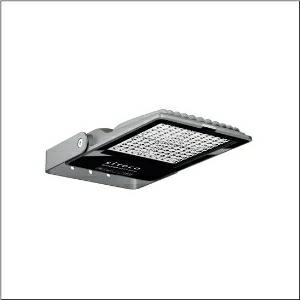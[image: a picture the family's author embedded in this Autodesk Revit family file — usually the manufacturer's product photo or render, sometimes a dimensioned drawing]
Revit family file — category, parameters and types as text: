
# Revit family: sicompact_r__31_mini___pl32_5xa7571b1k23_124a
name_source: partatom
category: Lighting Fixtures
units: mm (PartAtom-declared; Revit-internal decimal feet)

## family parameters
Cut with Voids When Loaded = No
Host = Face
Light Source = No
Part Type = Normal
Room Calculation Point = No
Round Connector Dimension = Use Diameter
Shared = No

## types (1)
- SiCompact® 31 mini  PL32 (1 x LED, 8000 lm, 48 W, 3000K)
    Apparent Load = 48 VA
    CIE Flux Codes = 32 69 98 100 100
    Color Rendering = 70
    Color Temperature = 3000K
    Default Elevation = 1800 mm
    Description = SiCompact® 31 mini, floodlight, primary light control with lens, of plastic, of toughened safety glass, transparent, light distribution: PL32, light emission: direct distribution, primary light characteristic: asymmetric, installation type: surface-mounted, LED, High Power LED, rated luminous flux: 8.000lm, luminous efficacy: 167lm/W, light colour: 730, colour temperature: 3000K, control gear: ON/OFF, with cable, 3x 1.5mm², mains connection: 220..240V, AC, 50/60Hz, connection cable pre-assembled, cable length: 2m, rated input power: 48W, of diecast aluminium, specular, metallic grey (RAL 9006), length: 461mm, width: 261mm, height: 62mm, bracket, of sheet steel, coated, metallic grey (RAL 9006), ON/OFF, protection rating (complete): IP66, insulation class (complete): insulation class I (protective earthing), certification: CE, ENEC, impact resistance: IK08, permissible operating ambient temperature: -40..+45°C, packaging unit: 1 piece

Light Distribution: PL32
    Height = 62 mm
    Lamp = 1 x LED
    Lamp Light Flux = 8000 lm
    Lamp Power = 48 W
    Lamp count = 1
    Length = 460 mm
    Luminous efficacy = 167 lm/W
    Manufacturer = Siteco
    ModVariant = No
    Model = 5XA7571B1K23
    Mounting Place = Wall
    Mounting Type = Surface mounted
    Number of Poles = 1
    OnlyDefault = Yes
    Power Factor = 1
    Product Name = SiCompact® 31 mini | PL32
    Product group = floodlight | wall mounted
    ProductGroupID = 2001
    Protection Class = Protection class I
    Protection Degree = IP 66
    RLX_Detail_Level = 1
    RLX_Emergency_Light_Flux = 0 lm
    RLX_Emergency_Type = 0
    RLX_Emergency_Type_DB = No
    RlxData = <blob elided: 126717 chars, md5=165bf783>
    Socket = socket
    Standby Power = 0 W
    System Light Flux = 8000 lm
    System Power = 48 W
    Type Comments = Product without accessories
    Type Image = l_1006951.jpg
    URL = http://relux.com
    VarID = ---
    Voltage = 0 V
    Weight = 0.00 kg
    Width = 260 mm

## geometry (parser evidence)
native form markers: Blend x4, Sweep x13
no freeform markers — native parametric forms only
